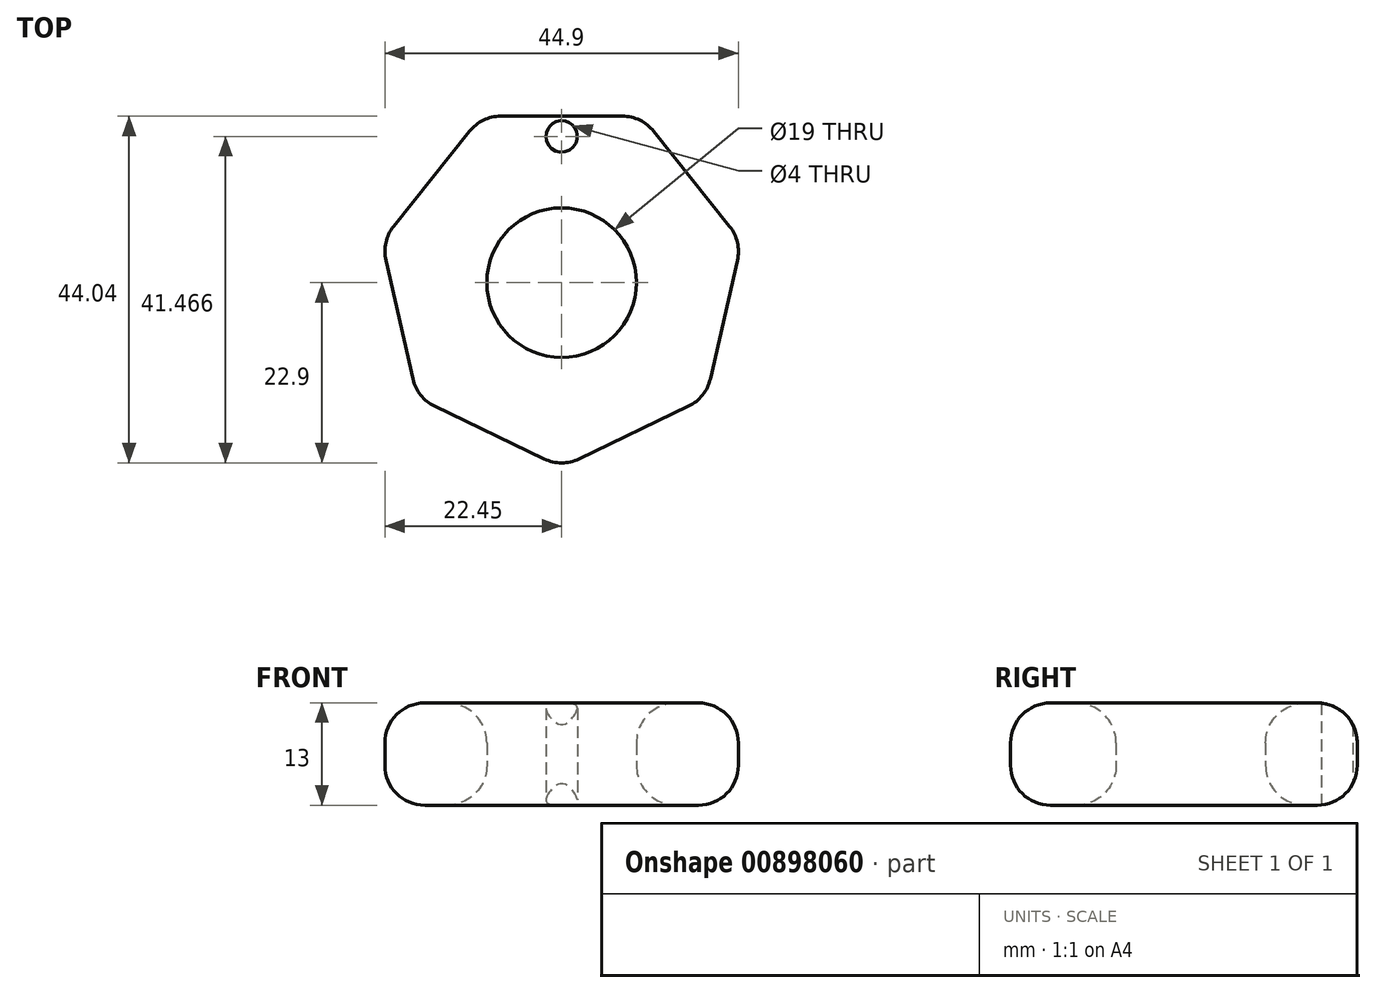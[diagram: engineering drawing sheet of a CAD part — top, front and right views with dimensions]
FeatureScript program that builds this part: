
annotation { "Feature Type Name" : "Feature", "Feature Type Description" : "" }
export const myFeature = defineFeature(function(context is Context, id is Id, definition is map)
    precondition{}
    {
        {
            var Q0;
            Q0=qCreatedBy(makeId("Top.planeOp"),FACE);
            var sketch = newSketch(context, id + "F0", { "sketchPlane" : qUnion([Q0])});
            skCircle(sketch, "E0.cCircle", {"center": v(0, 0) * mm, "radius": 21.14 * mm, "construction": true});
            skLineSegment(sketch, "E0.0", {"start": v(-10.18, 21.14) * mm, "end": v(10.18, 21.14) * mm});
            skLineSegment(sketch, "E0.1", {"start": v(10.18, 21.14) * mm, "end": v(22.87, 5.22) * mm});
            skLineSegment(sketch, "E0.2", {"start": v(22.87, 5.22) * mm, "end": v(18.34, -14.63) * mm});
            skLineSegment(sketch, "E0.3", {"start": v(18.34, -14.63) * mm, "end": v(0, -23.46) * mm});
            skLineSegment(sketch, "E0.4", {"start": v(0, -23.46) * mm, "end": v(-18.34, -14.63) * mm});
            skLineSegment(sketch, "E0.5", {"start": v(-18.34, -14.63) * mm, "end": v(-22.87, 5.22) * mm});
            skLineSegment(sketch, "E0.6", {"start": v(-22.87, 5.22) * mm, "end": v(-10.18, 21.14) * mm});
            skPoint(sketch, "E0.0.midPoint", {"position": v(0, 21.14) * mm});
            skCircle(sketch, "E1", {"center": v(0, 0) * mm, "radius": 9.5 * mm});
            skSolve(sketch);
        }
        {
            var Q0;
            Q0 = qSketchRegion(id + "F0", true);
            extrude(context, id + "F1", {"entities" : qUnion([Q0]), "depth" : 13 * mm, "offsetDistance" : 25.4 * mm});
        }
        {
            var Q0;
            Q0=makeQuery(id+"F1.opExtrude","CAP_EDGE",EDGE,{"disambiguationData":[OSD([sQuery(id+"F0.wireOp",EDGE,"E1")])],"isStart":true});
            var Q1;
            Q1=makeQuery(id+"F1.opExtrude","CAP_EDGE",EDGE,{"disambiguationData":[OSD([sQuery(id+"F0.wireOp",EDGE,"E1")])],"isStart":false});
            var Q2;
            Q2=makeQuery(id+"F1.opExtrude","SWEPT_FACE",FACE,{"disambiguationData":[OSD([sQuery(id+"F0.wireOp",EDGE,"E0.6")])]});
            var Q3;
            Q3=makeQuery(id+"F1.opExtrude","SWEPT_FACE",FACE,{"disambiguationData":[OSD([sQuery(id+"F0.wireOp",EDGE,"E0.5")])]});
            var Q4;
            Q4=makeQuery(id+"F1.opExtrude","SWEPT_FACE",FACE,{"disambiguationData":[OSD([sQuery(id+"F0.wireOp",EDGE,"E0.4")])]});
            var Q5;
            Q5=makeQuery(id+"F1.opExtrude","SWEPT_FACE",FACE,{"disambiguationData":[OSD([sQuery(id+"F0.wireOp",EDGE,"E0.3")])]});
            var Q6;
            Q6=makeQuery(id+"F1.opExtrude","SWEPT_FACE",FACE,{"disambiguationData":[OSD([sQuery(id+"F0.wireOp",EDGE,"E0.2")])]});
            var Q7;
            Q7=makeQuery(id+"F1.opExtrude","SWEPT_FACE",FACE,{"disambiguationData":[OSD([sQuery(id+"F0.wireOp",EDGE,"E0.1")])]});
            var Q8;
            Q8=makeQuery(id+"F1.opExtrude","SWEPT_FACE",FACE,{"disambiguationData":[OSD([sQuery(id+"F0.wireOp",EDGE,"E0.0")])]});
            fillet(context, id + "F2", {"entities" : qUnion([Q0, Q1, Q2, Q3, Q4, Q5, Q6, Q7, Q8]), "radius" : 5.08 * mm, "tangentPropagation" : true, "allowEdgeOverflow" : false});
        }
        {
            var Q0;
            Q0=qCreatedBy(makeId("Top.planeOp"),FACE);
            var sketch = newSketch(context, id + "F3", { "sketchPlane" : qUnion([Q0])});
            skCircle(sketch, "E2", {"center": v(0, 18.57) * mm, "radius": 1.5 * mm});
            skSolve(sketch);
        }
        {
            var Q0;
            Q0=sQuery(id+"F3.wireOp",VERTEX,"E2.center");
            var Q1;
            Q1=makeQuery(id+"F1.opExtrude","SWEPT_BODY",BODY,{"disambiguationData":[OSD([sQuery(id+"F0.wireOp",EDGE,"E0.0"),sQuery(id+"F0.wireOp",EDGE,"E0.1"),sQuery(id+"F0.wireOp",EDGE,"E0.2"),sQuery(id+"F0.wireOp",EDGE,"E0.3"),sQuery(id+"F0.wireOp",EDGE,"E0.4"),sQuery(id+"F0.wireOp",EDGE,"E0.5"),sQuery(id+"F0.wireOp",EDGE,"E0.6"),sQuery(id+"F0.wireOp",EDGE,"E1")])]});
            hole(context, id + "F4", {"style" : HoleStyle.SIMPLE, "endStyle" : HoleEndStyle.THROUGH, "oppositeDirection" : true, "holeDiameter" : 4 * mm, "majorDiameter" : 6.35 * mm, "isTappedThrough" : true, "tappedDepth" : 12.7 * mm, "tapClearance" : 3, "locations" : qUnion([Q0]), "scope" : qUnion([Q1])});
        }
    });
